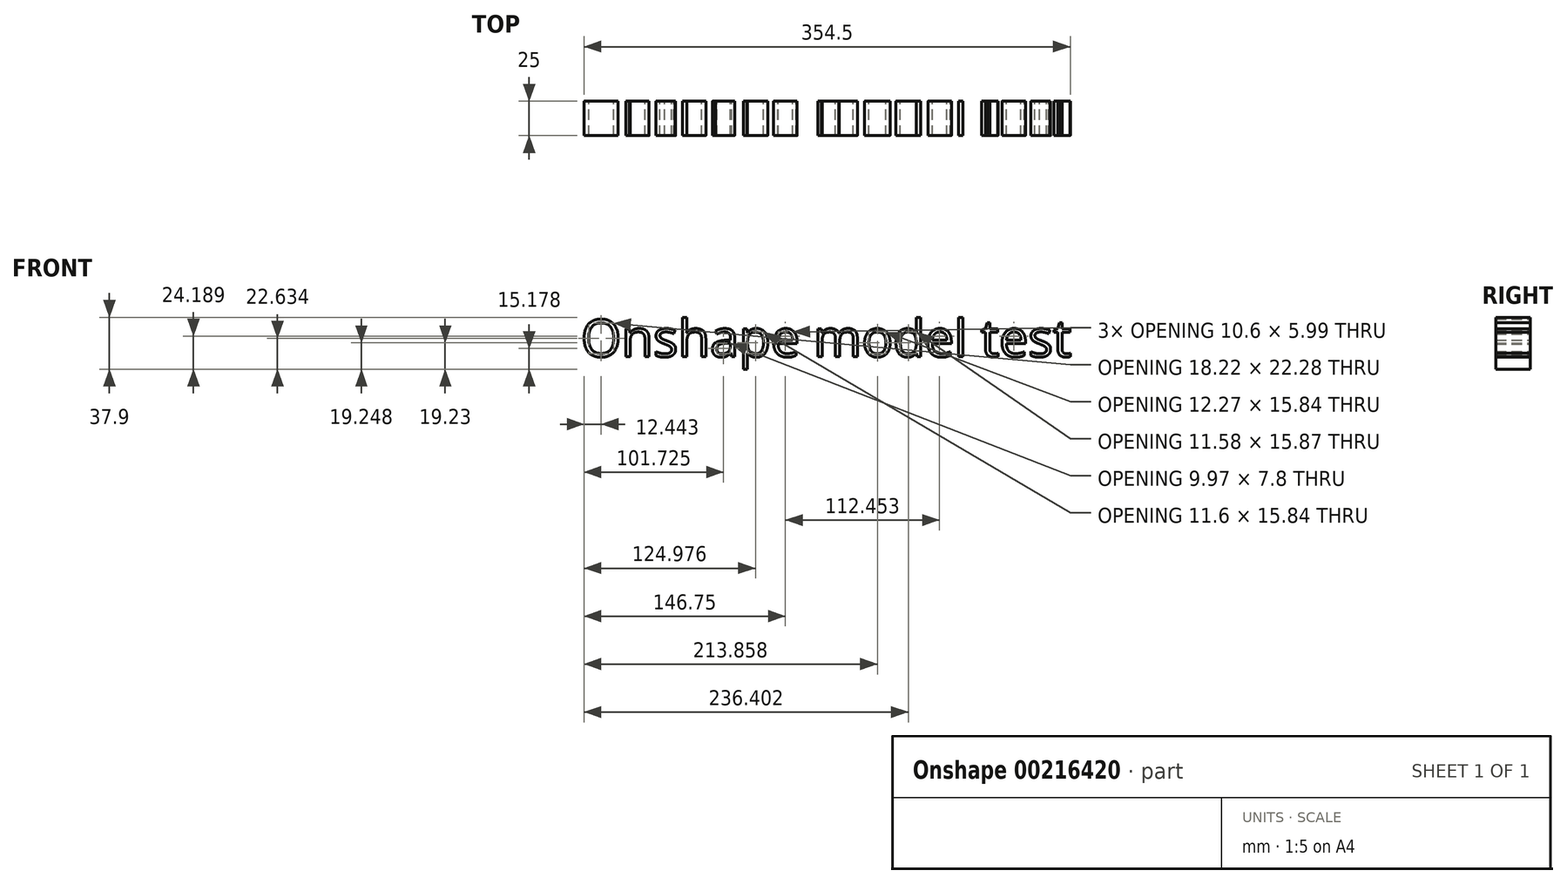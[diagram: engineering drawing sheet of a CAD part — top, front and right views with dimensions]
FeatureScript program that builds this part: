
annotation { "Feature Type Name" : "Feature", "Feature Type Description" : "" }
export const myFeature = defineFeature(function(context is Context, id is Id, definition is map)
    precondition{}
    {
        {
            var Q0;
            Q0=qCreatedBy(makeId("Front.planeOp"),FACE);
            var sketch = newSketch(context, id + "F0", { "sketchPlane" : qUnion([Q0])});
            skText(sketch, "E0", { "text": "Onshape model test", "fontName": "OpenSans-Regular.ttf"});
            const initialGuessF0  = {"E0": [0, 0, 1, 0, 0.02728]};
            skSetInitialGuess(sketch, initialGuessF0);
            skSolve(sketch);
        }
        {
            var Q0;
            Q0=makeQuery(id+"F0.imprint","IMPRINT",FACE,{"disambiguationData":[TD([[makeQuery(id+"F0.imprint","IMPRINT",EDGE,{"derivedFrom":sQuery(id+"F0.wireOp",EDGE,"E0.sketch_text.stroke-175")}),-1.0]])]});
            var Q1;
            Q1=makeQuery(id+"F0.imprint","IMPRINT",FACE,{"disambiguationData":[TD([[makeQuery(id+"F0.imprint","IMPRINT",EDGE,{"derivedFrom":sQuery(id+"F0.wireOp",EDGE,"E0.sketch_text.stroke-147")}),-1.0]])]});
            var Q2;
            Q2=makeQuery(id+"F0.imprint","IMPRINT",FACE,{"disambiguationData":[TD([[makeQuery(id+"F0.imprint","IMPRINT",EDGE,{"derivedFrom":sQuery(id+"F0.wireOp",EDGE,"E0.sketch_text.stroke-128")}),-1.0]])]});
            var Q3;
            Q3=makeQuery(id+"F0.imprint","IMPRINT",FACE,{"disambiguationData":[TD([[makeQuery(id+"F0.imprint","IMPRINT",EDGE,{"derivedFrom":sQuery(id+"F0.wireOp",EDGE,"E0.sketch_text.stroke-0")}),-1.0]])]});
            var Q4;
            Q4=makeQuery(id+"F0.imprint","IMPRINT",FACE,{"disambiguationData":[TD([[makeQuery(id+"F0.imprint","IMPRINT",EDGE,{"derivedFrom":sQuery(id+"F0.wireOp",EDGE,"E0.sketch_text.stroke-16")}),-1.0]])]});
            var Q5;
            Q5=makeQuery(id+"F0.imprint","IMPRINT",FACE,{"disambiguationData":[TD([[makeQuery(id+"F0.imprint","IMPRINT",EDGE,{"derivedFrom":sQuery(id+"F0.wireOp",EDGE,"E0.sketch_text.stroke-33")}),-1.0]])]});
            var Q6;
            Q6=makeQuery(id+"F0.imprint","IMPRINT",FACE,{"disambiguationData":[TD([[makeQuery(id+"F0.imprint","IMPRINT",EDGE,{"derivedFrom":sQuery(id+"F0.wireOp",EDGE,"E0.sketch_text.stroke-58")}),-1.0]])]});
            var Q7;
            Q7=makeQuery(id+"F0.imprint","IMPRINT",FACE,{"disambiguationData":[TD([[makeQuery(id+"F0.imprint","IMPRINT",EDGE,{"derivedFrom":sQuery(id+"F0.wireOp",EDGE,"E0.sketch_text.stroke-76")}),-1.0]])]});
            var Q8;
            Q8=makeQuery(id+"F0.imprint","IMPRINT",FACE,{"disambiguationData":[TD([[makeQuery(id+"F0.imprint","IMPRINT",EDGE,{"derivedFrom":sQuery(id+"F0.wireOp",EDGE,"E0.sketch_text.stroke-103")}),-1.0]])]});
            var Q9;
            Q9=makeQuery(id+"F0.imprint","IMPRINT",FACE,{"disambiguationData":[TD([[makeQuery(id+"F0.imprint","IMPRINT",EDGE,{"derivedFrom":sQuery(id+"F0.wireOp",EDGE,"E0.sketch_text.stroke-192")}),-1.0]])]});
            var Q10;
            Q10=makeQuery(id+"F0.imprint","IMPRINT",FACE,{"disambiguationData":[TD([[makeQuery(id+"F0.imprint","IMPRINT",EDGE,{"derivedFrom":sQuery(id+"F0.wireOp",EDGE,"E0.sketch_text.stroke-216")}),-1.0]])]});
            var Q11;
            Q11=makeQuery(id+"F0.imprint","IMPRINT",FACE,{"disambiguationData":[TD([[makeQuery(id+"F0.imprint","IMPRINT",EDGE,{"derivedFrom":sQuery(id+"F0.wireOp",EDGE,"E0.sketch_text.stroke-235")}),-1.0]])]});
            var Q12;
            Q12=makeQuery(id+"F0.imprint","IMPRINT",FACE,{"disambiguationData":[TD([[makeQuery(id+"F0.imprint","IMPRINT",EDGE,{"derivedFrom":sQuery(id+"F0.wireOp",EDGE,"E0.sketch_text.stroke-239")}),-1.0]])]});
            var Q13;
            Q13=makeQuery(id+"F0.imprint","IMPRINT",FACE,{"disambiguationData":[TD([[makeQuery(id+"F0.imprint","IMPRINT",EDGE,{"derivedFrom":sQuery(id+"F0.wireOp",EDGE,"E0.sketch_text.stroke-258")}),-1.0]])]});
            var Q14;
            Q14=makeQuery(id+"F0.imprint","IMPRINT",FACE,{"disambiguationData":[TD([[makeQuery(id+"F0.imprint","IMPRINT",EDGE,{"derivedFrom":sQuery(id+"F0.wireOp",EDGE,"E0.sketch_text.stroke-277")}),-1.0]])]});
            var Q15;
            Q15=makeQuery(id+"F0.imprint","IMPRINT",FACE,{"disambiguationData":[TD([[makeQuery(id+"F0.imprint","IMPRINT",EDGE,{"derivedFrom":sQuery(id+"F0.wireOp",EDGE,"E0.sketch_text.stroke-302")}),-1.0]])]});
            extrude(context, id + "F1", {"entities" : qUnion([Q0, Q1, Q2, Q3, Q4, Q5, Q6, Q7, Q8, Q9, Q10, Q11, Q12, Q13, Q14, Q15]), "depth" : 25 * mm});
        }
    });
